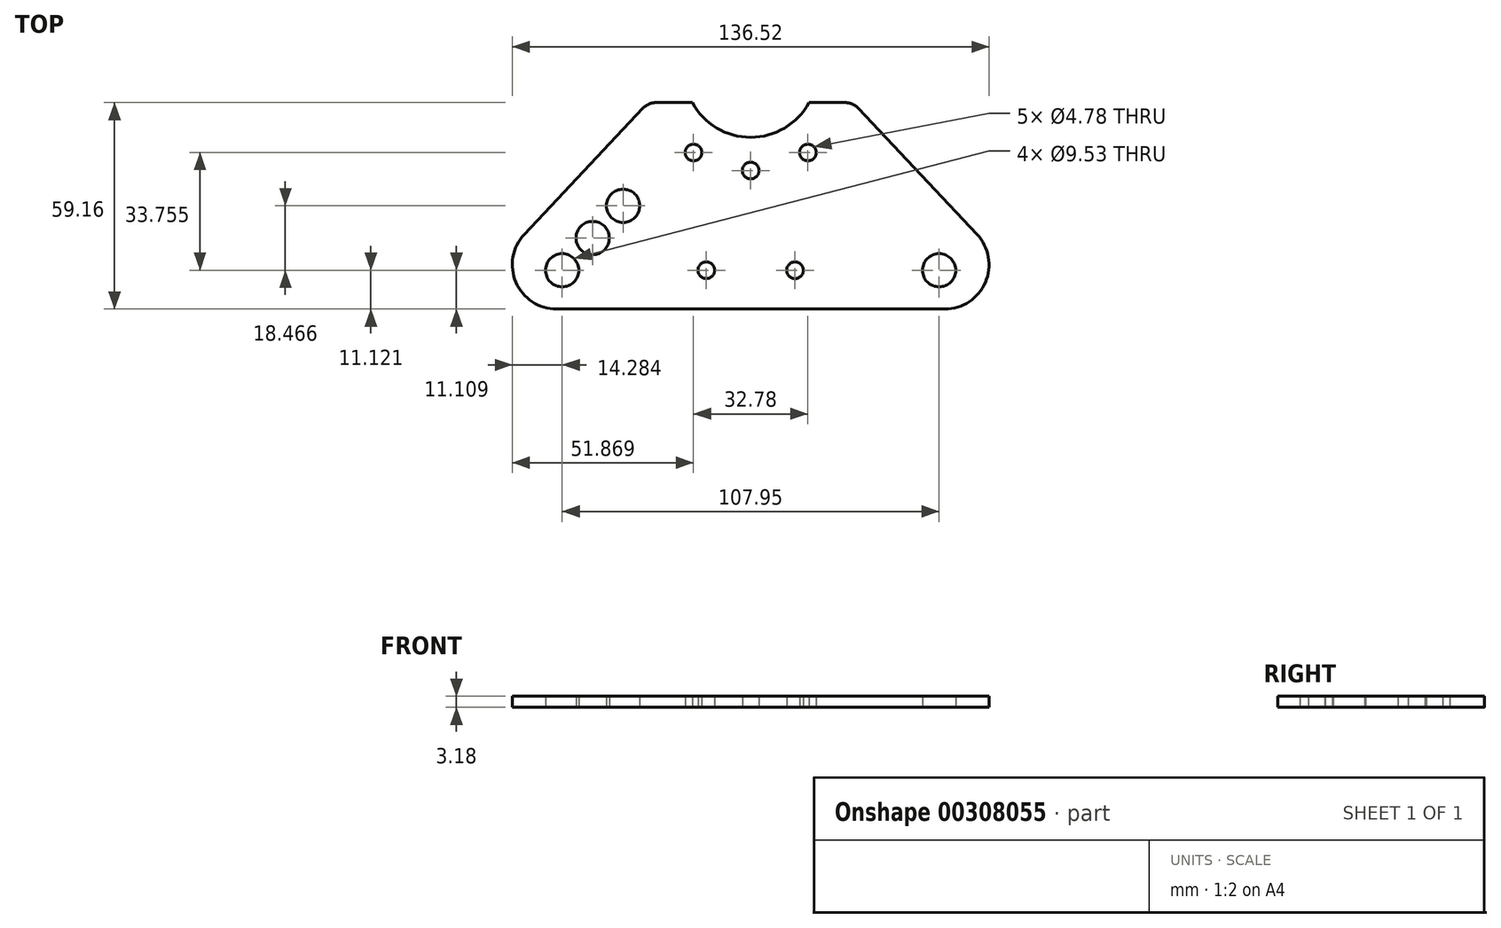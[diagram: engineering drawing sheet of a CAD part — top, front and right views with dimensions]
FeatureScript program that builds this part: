
annotation { "Feature Type Name" : "Feature", "Feature Type Description" : "" }
export const myFeature = defineFeature(function(context is Context, id is Id, definition is map)
    precondition{}
    {
        {
            var Q0;
            Q0=qCreatedBy(makeId("Top.planeOp"),FACE);
            var sketch = newSketch(context, id + "F0", { "sketchPlane" : qUnion([Q0])});
            skArc(sketch, "E0", {"start": v(6.68, 19.07) * mm, "mid": v(16.4, 21.74) * mm, "end": v(23.4, 29) * mm});
            skArc(sketch, "E1.MirrorCS", {"start": v(6.68, 19.07) * mm, "mid": v(-3.05, 21.74) * mm, "end": v(-10.05, 29) * mm});
            skArc(sketch, "E2.MirrorCS", {"start": v(-48.88, -30.15) * mm, "mid": v(-60.54, -22.5) * mm, "end": v(-58.14, -8.76) * mm});
            skLineSegment(sketch, "E3.MirrorCS", {"start": v(6.68, -30.15) * mm, "end": v(-48.88, -30.15) * mm});
            skCircle(sketch, "E4", {"center": v(-47.3, -19.03) * mm, "radius": 4.76 * mm});
            skCircle(sketch, "E5", {"center": v(-6.02, -19.03) * mm, "radius": 2.39 * mm});
            skCircle(sketch, "E6.MirrorC", {"center": v(19.38, -19.04) * mm, "radius": 2.39 * mm});
            skPoint(sketch, "E7.orphan", {"position": v(-58.1, -10.28) * mm});
            skCircle(sketch, "E8", {"center": v(6.68, 9.55) * mm, "radius": 2.39 * mm});
            skCircle(sketch, "E9.2.0", {"center": v(-9.71, 14.71) * mm, "radius": 2.39 * mm});
            skCircle(sketch, "E10.MirrorC", {"center": v(23.07, 14.71) * mm, "radius": 2.39 * mm});
            skLineSegment(sketch, "E11", {"start": v(6.68, 38.12) * mm, "end": v(6.68, 9.55) * mm, "construction": true});
            skLineSegment(sketch, "E12", {"start": v(-47.3, -19.03) * mm, "end": v(92.76, -19.03) * mm, "construction": true});
            skLineSegment(sketch, "E13.MirrorCS", {"start": v(6.68, -30.15) * mm, "end": v(62.24, -30.15) * mm});
            skArc(sketch, "E14.MirrorCS", {"start": v(62.24, -30.15) * mm, "mid": v(73.9, -22.5) * mm, "end": v(71.5, -8.76) * mm});
            skCircle(sketch, "E15", {"center": v(60.65, -19.03) * mm, "radius": 4.76 * mm});
            skLineSegment(sketch, "E16", {"start": v(-47.3, -19.03) * mm, "end": v(6.68, 38.12) * mm, "construction": true});
            skLineSegment(sketch, "E17", {"start": v(6.68, 38.12) * mm, "end": v(60.65, -19.03) * mm, "construction": true});
            skCircle(sketch, "E18", {"center": v(-38.58, -9.8) * mm, "radius": 4.76 * mm});
            skCircle(sketch, "E19", {"center": v(-29.86, -0.56) * mm, "radius": 4.76 * mm});
            skLineSegment(sketch, "E20.0", {"start": v(23.4, 29) * mm, "end": v(36.04, 29) * mm});
            skLineSegment(sketch, "E21.0", {"start": v(-10.05, 29) * mm, "end": v(-22.68, 29) * mm});
            skLineSegment(sketch, "E22", {"start": v(-22.68, 29) * mm, "end": v(-58.14, -8.76) * mm});
            skLineSegment(sketch, "E23", {"start": v(71.5, -8.76) * mm, "end": v(36.04, 29) * mm});
            skSolve(sketch);
        }
        {
            var Q0;
            Q0 = qSketchRegion(id + "F0", true);
            extrude(context, id + "F1", {"entities" : qUnion([Q0]), "endBound" : BoundingType.SYMMETRIC, "depth" : 3.17 * mm, "offsetDistance" : 25.4 * mm});
        }
        {
            var Q0;
            Q0=makeQuery(id+"F1.opExtrude","SWEPT_EDGE",EDGE,{"disambiguationData":[OSD([sQuery(id+"F0.wireOp",EDGE,"E21.0"),sQuery(id+"F0.wireOp",EDGE,"E22")])]});
            var Q1;
            Q1=makeQuery(id+"F1.opExtrude","SWEPT_EDGE",EDGE,{"disambiguationData":[OSD([sQuery(id+"F0.wireOp",EDGE,"E20.0"),sQuery(id+"F0.wireOp",EDGE,"E23")])]});
            fillet(context, id + "F2", {"entities" : qUnion([Q0, Q1]), "tangentPropagation" : true, "radius" : 5.08 * mm, "defaultsChanged" : false, "vertexSettings" : [], "allowEdgeOverflow" : false});
        }
    });
